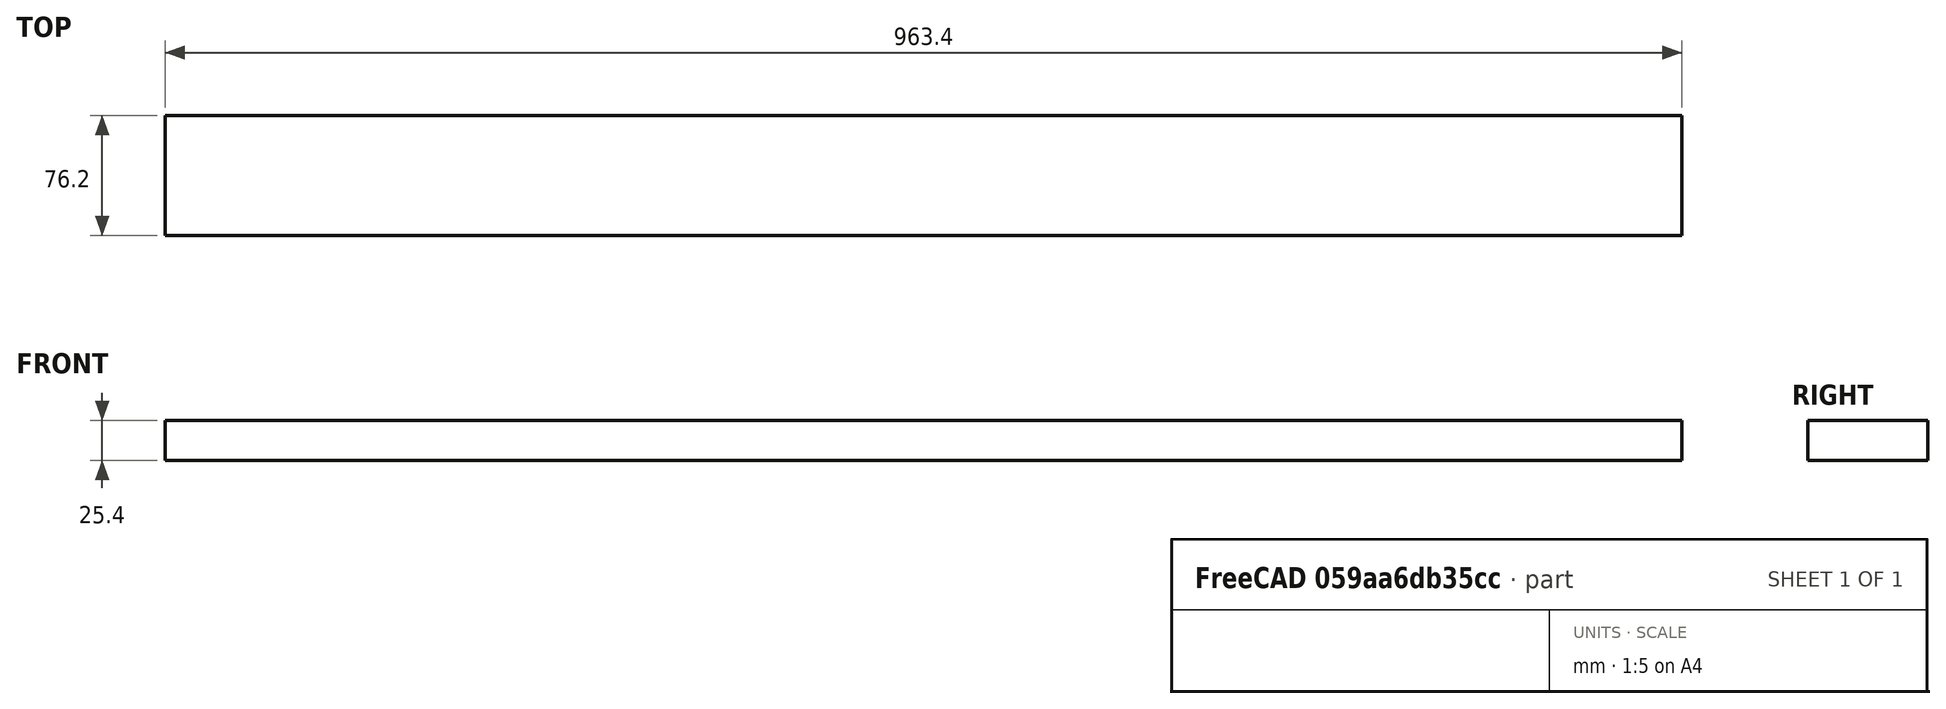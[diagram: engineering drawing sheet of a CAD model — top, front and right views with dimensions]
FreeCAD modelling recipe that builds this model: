
FCSTD DOCUMENT  (FreeCAD 0.19R24276 (Git))
Label: cover front and back
License: All rights reserved
LicenseURL: http://en.wikipedia.org/wiki/All_rights_reserved
objects: Sketcher::SketchObject×1, PartDesign::Pad×1, PartDesign::Body×1
note: 4 computed .brp shape members not serialized (recipe doc carries the construction recipe); baked Part::Feature solids carry a one-line shape summary decoded from their .brp

FEATURE [Sketcher::SketchObject] Sketch
  FullyConstrained = true
  MapMode = 5
  Support = -> [XY_Plane]
  sketch-geometry (4):
    g0: LineSegment StartX=0 StartY=0 StartZ=0 EndX=963.4 EndY=0 EndZ=0
    g1: LineSegment StartX=963.4 StartY=0 StartZ=0 EndX=963.4 EndY=-76.2 EndZ=0
    g2: LineSegment StartX=963.4 StartY=-76.2 StartZ=0 EndX=0 EndY=-76.2 EndZ=0
    g3: LineSegment StartX=0 StartY=-76.2 StartZ=0 EndX=0 EndY=0 EndZ=0
  constraints (11):
    c: Coincident(g0,g1)
    c: Coincident(g1,g2)
    c: Coincident(g2,g3)
    c: Coincident(g3,g0)
    c: Horizontal(g0)
    c: Horizontal(g2)
    c: Vertical(g1)
    c: Vertical(g3)
    c: Coincident(g0,g-1)
    c: DistanceY(g1,g1) = 76.2
    c: DistanceX(g0,g0) = 963.4
FEATURE [PartDesign::Pad] Pad
  Direction = (1,1,1)
  Length = 25.4
  Length2 = 100
  Profile = -> Sketch
  Type = 0
FEATURE [PartDesign::Body] Body
  Group = -> [Sketch,Pad]
  Origin = -> Origin
  Tip = -> Pad
